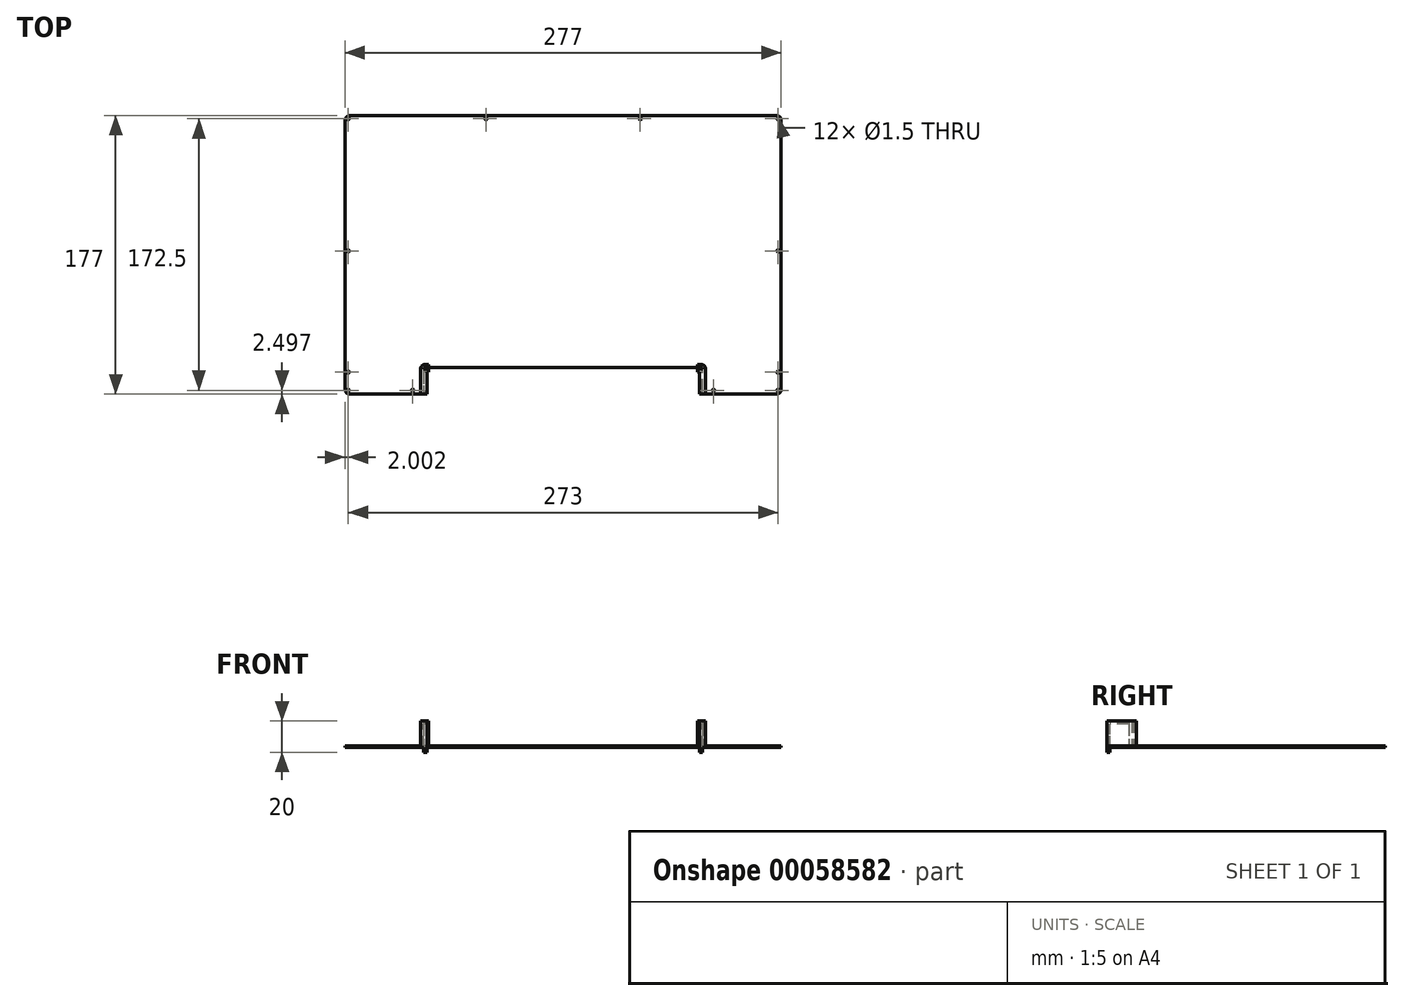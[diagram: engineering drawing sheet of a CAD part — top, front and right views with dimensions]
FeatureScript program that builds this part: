
annotation { "Feature Type Name" : "Feature", "Feature Type Description" : "" }
export const myFeature = defineFeature(function(context is Context, id is Id, definition is map)
    precondition{}
    {
        {
            var Q0;
            Q0=qCreatedBy(makeId("Top.planeOp"),FACE);
            var sketch = newSketch(context, id + "F0", { "sketchPlane" : qUnion([Q0])});
            skLineSegment(sketch, "E0.0.0", {"start": v(88.9, -46.67) * mm, "end": v(88.9, -105.67) * mm});
            skLineSegment(sketch, "E0.0.1", {"start": v(88.9, -105.67) * mm, "end": v(-89.1, -105.67) * mm});
            skLineSegment(sketch, "E0.0.2", {"start": v(-89.1, -105.67) * mm, "end": v(-89.1, -46.67) * mm});
            skLineSegment(sketch, "E0.0.3", {"start": v(-89.1, -46.67) * mm, "end": v(-86.1, -46.67) * mm});
            skLineSegment(sketch, "E0.0.4", {"start": v(-86.1, -46.67) * mm, "end": v(-86.1, -44.67) * mm});
            skLineSegment(sketch, "E0.0.5", {"start": v(-86.1, -44.67) * mm, "end": v(-89.1, -44.67) * mm});
            skLineSegment(sketch, "E0.0.6", {"start": v(-89.1, -44.67) * mm, "end": v(-89.1, -42.67) * mm});
            skLineSegment(sketch, "E0.0.7", {"start": v(-89.1, -42.67) * mm, "end": v(-86.1, -42.67) * mm});
            skLineSegment(sketch, "E0.0.8", {"start": v(-86.1, -42.67) * mm, "end": v(-86.1, -40.67) * mm});
            skLineSegment(sketch, "E0.0.9", {"start": v(-86.1, -40.67) * mm, "end": v(-91.1, -40.67) * mm});
            skLineSegment(sketch, "E0.0.10", {"start": v(-91.1, -40.67) * mm, "end": v(-91.1, -59.67) * mm});
            skLineSegment(sketch, "E0.0.11", {"start": v(-91.1, -59.67) * mm, "end": v(-137.1, -59.67) * mm});
            skLineSegment(sketch, "E0.0.12", {"start": v(-137.1, -59.67) * mm, "end": v(-137.1, -107.67) * mm});
            skLineSegment(sketch, "E0.0.13", {"start": v(-137.1, -107.67) * mm, "end": v(136.9, -107.67) * mm});
            skLineSegment(sketch, "E0.0.14", {"start": v(136.9, -107.67) * mm, "end": v(136.9, -59.67) * mm});
            skLineSegment(sketch, "E0.0.15", {"start": v(136.9, -59.67) * mm, "end": v(90.9, -59.67) * mm});
            skLineSegment(sketch, "E0.0.16", {"start": v(90.9, -59.67) * mm, "end": v(90.9, -40.67) * mm});
            skLineSegment(sketch, "E0.0.17", {"start": v(90.9, -40.67) * mm, "end": v(85.9, -40.67) * mm});
            skLineSegment(sketch, "E0.0.18", {"start": v(85.9, -40.67) * mm, "end": v(85.9, -42.67) * mm});
            skLineSegment(sketch, "E0.0.19", {"start": v(85.9, -42.67) * mm, "end": v(88.9, -42.67) * mm});
            skLineSegment(sketch, "E0.0.20", {"start": v(88.9, -42.67) * mm, "end": v(88.9, -44.67) * mm});
            skLineSegment(sketch, "E0.0.21", {"start": v(88.9, -44.67) * mm, "end": v(85.9, -44.67) * mm});
            skLineSegment(sketch, "E0.0.22", {"start": v(85.9, -44.67) * mm, "end": v(85.9, -46.67) * mm});
            skLineSegment(sketch, "E0.0.23", {"start": v(85.9, -46.67) * mm, "end": v(88.9, -46.67) * mm});
            skLineSegment(sketch, "E1.0.0", {"start": v(134.9, -59.67) * mm, "end": v(136.9, -59.67) * mm});
            skLineSegment(sketch, "E1.0.1", {"start": v(136.9, -59.67) * mm, "end": v(136.9, 110.83) * mm});
            skLineSegment(sketch, "E1.0.2", {"start": v(136.9, 110.83) * mm, "end": v(-137.1, 110.83) * mm});
            skLineSegment(sketch, "E1.0.3", {"start": v(-137.1, 110.83) * mm, "end": v(-137.1, -59.67) * mm});
            skLineSegment(sketch, "E1.0.4", {"start": v(-137.1, -59.67) * mm, "end": v(-135.1, -59.67) * mm});
            skLineSegment(sketch, "E1.0.5", {"start": v(-135.1, -59.67) * mm, "end": v(-135.1, -52.17) * mm});
            skLineSegment(sketch, "E1.0.6", {"start": v(-135.1, -52.17) * mm, "end": v(-130.1, -52.17) * mm});
            skLineSegment(sketch, "E1.0.7", {"start": v(-130.1, -52.17) * mm, "end": v(-130.1, -50.17) * mm});
            skLineSegment(sketch, "E1.0.8", {"start": v(-130.1, -50.17) * mm, "end": v(-134.1, -50.17) * mm});
            skLineSegment(sketch, "E1.0.9", {"start": v(-134.1, -50.17) * mm, "end": v(-134.1, -47.17) * mm});
            skLineSegment(sketch, "E1.0.10", {"start": v(-134.1, -47.17) * mm, "end": v(-135.1, -47.17) * mm});
            skLineSegment(sketch, "E1.0.11", {"start": v(-135.1, -47.17) * mm, "end": v(-135.1, 25.83) * mm});
            skLineSegment(sketch, "E1.0.12", {"start": v(-135.1, 25.83) * mm, "end": v(-134.1, 25.83) * mm});
            skLineSegment(sketch, "E1.0.13", {"start": v(-134.1, 25.83) * mm, "end": v(-134.1, 30.83) * mm});
            skLineSegment(sketch, "E1.0.14", {"start": v(-134.1, 30.83) * mm, "end": v(-135.1, 30.83) * mm});
            skLineSegment(sketch, "E1.0.15", {"start": v(-135.1, 30.83) * mm, "end": v(-135.1, 103.83) * mm});
            skLineSegment(sketch, "E1.0.16", {"start": v(-135.1, 103.83) * mm, "end": v(-134.1, 103.83) * mm});
            skLineSegment(sketch, "E1.0.17", {"start": v(-134.1, 103.83) * mm, "end": v(-134.1, 106.83) * mm});
            skLineSegment(sketch, "E1.0.18", {"start": v(-134.1, 106.83) * mm, "end": v(-129.1, 106.83) * mm});
            skLineSegment(sketch, "E1.0.19", {"start": v(-129.1, 106.83) * mm, "end": v(-129.1, 108.83) * mm});
            skLineSegment(sketch, "E1.0.20", {"start": v(-129.1, 108.83) * mm, "end": v(-50.1, 108.83) * mm});
            skLineSegment(sketch, "E1.0.21", {"start": v(-50.1, 108.83) * mm, "end": v(-50.1, 106.83) * mm});
            skLineSegment(sketch, "E1.0.22", {"start": v(-50.1, 106.83) * mm, "end": v(-45.1, 106.83) * mm});
            skLineSegment(sketch, "E1.0.23", {"start": v(-45.1, 106.83) * mm, "end": v(-45.1, 108.83) * mm});
            skLineSegment(sketch, "E1.0.24", {"start": v(-45.1, 108.83) * mm, "end": v(44.9, 108.83) * mm});
            skLineSegment(sketch, "E1.0.25", {"start": v(44.9, 108.83) * mm, "end": v(44.9, 106.83) * mm});
            skLineSegment(sketch, "E1.0.26", {"start": v(44.9, 106.83) * mm, "end": v(49.9, 106.83) * mm});
            skLineSegment(sketch, "E1.0.27", {"start": v(49.9, 106.83) * mm, "end": v(49.9, 108.83) * mm});
            skLineSegment(sketch, "E1.0.28", {"start": v(49.9, 108.83) * mm, "end": v(128.9, 108.83) * mm});
            skLineSegment(sketch, "E1.0.29", {"start": v(128.9, 108.83) * mm, "end": v(128.9, 106.83) * mm});
            skLineSegment(sketch, "E1.0.30", {"start": v(128.9, 106.83) * mm, "end": v(133.9, 106.83) * mm});
            skLineSegment(sketch, "E1.0.31", {"start": v(133.9, 106.83) * mm, "end": v(133.9, 103.83) * mm});
            skLineSegment(sketch, "E1.0.32", {"start": v(133.9, 103.83) * mm, "end": v(134.9, 103.83) * mm});
            skLineSegment(sketch, "E1.0.33", {"start": v(134.9, 103.83) * mm, "end": v(134.9, 30.83) * mm});
            skLineSegment(sketch, "E1.0.34", {"start": v(134.9, 30.83) * mm, "end": v(133.9, 30.83) * mm});
            skLineSegment(sketch, "E1.0.35", {"start": v(133.9, 30.83) * mm, "end": v(133.9, 25.83) * mm});
            skLineSegment(sketch, "E1.0.36", {"start": v(133.9, 25.83) * mm, "end": v(134.9, 25.83) * mm});
            skLineSegment(sketch, "E1.0.37", {"start": v(134.9, 25.83) * mm, "end": v(134.9, -47.17) * mm});
            skLineSegment(sketch, "E1.0.38", {"start": v(134.9, -47.17) * mm, "end": v(133.9, -47.17) * mm});
            skLineSegment(sketch, "E1.0.39", {"start": v(133.9, -47.17) * mm, "end": v(133.9, -50.17) * mm});
            skLineSegment(sketch, "E1.0.40", {"start": v(133.9, -50.17) * mm, "end": v(129.9, -50.17) * mm});
            skLineSegment(sketch, "E1.0.41", {"start": v(129.9, -50.17) * mm, "end": v(129.9, -52.17) * mm});
            skLineSegment(sketch, "E1.0.42", {"start": v(129.9, -52.17) * mm, "end": v(134.9, -52.17) * mm});
            skLineSegment(sketch, "E1.0.43", {"start": v(134.9, -52.17) * mm, "end": v(134.9, -59.67) * mm});
            skLineSegment(sketch, "E2", {"start": v(-89.1, -105.67) * mm, "end": v(-89.1, -107.67) * mm});
            skLineSegment(sketch, "E3", {"start": v(88.9, -105.67) * mm, "end": v(88.9, -107.67) * mm});
            skSolve(sketch);
        }
        {
            var Q0;
            Q0=qCreatedBy(makeId("Top.planeOp"),FACE);
            var sketch = newSketch(context, id + "F1", { "sketchPlane" : qUnion([Q0])});
            skPoint(sketch, "E4.0", {"position": v(-91.1, -59.67) * mm});
            skPoint(sketch, "E5.0", {"position": v(-91.1, -40.67) * mm});
            skPoint(sketch, "E6.0", {"position": v(-86.1, -40.67) * mm});
            skPoint(sketch, "E7.0", {"position": v(-86.1, -42.67) * mm});
            skPoint(sketch, "E8.0", {"position": v(-89.1, -42.67) * mm});
            skPoint(sketch, "E9.0", {"position": v(-89.1, -46.67) * mm});
            skLineSegment(sketch, "E10", {"start": v(-91.1, -59.67) * mm, "end": v(-91.1, -40.67) * mm});
            skLineSegment(sketch, "E11", {"start": v(-91.1, -40.67) * mm, "end": v(-86.1, -40.67) * mm});
            skLineSegment(sketch, "E12", {"start": v(-86.1, -40.67) * mm, "end": v(-86.1, -42.67) * mm});
            skLineSegment(sketch, "E13", {"start": v(-86.1, -42.67) * mm, "end": v(-89.1, -42.67) * mm});
            skLineSegment(sketch, "E14", {"start": v(-89.1, -42.67) * mm, "end": v(-89.1, -43.67) * mm});
            skLineSegment(sketch, "E15", {"start": v(-89.1, -43.67) * mm, "end": v(-86.1, -43.67) * mm});
            skLineSegment(sketch, "E16", {"start": v(-86.1, -43.67) * mm, "end": v(-86.1, -45.67) * mm});
            skLineSegment(sketch, "E17", {"start": v(-86.1, -45.67) * mm, "end": v(-89.1, -45.67) * mm});
            skLineSegment(sketch, "E18", {"start": v(-89.1, -45.67) * mm, "end": v(-89.1, -59.67) * mm});
            skLineSegment(sketch, "E19", {"start": v(-89.1, -59.67) * mm, "end": v(-91.1, -59.67) * mm});
            skLineSegment(sketch, "E20", {"start": v(-89.1, -59.67) * mm, "end": v(-0.6, -59.67) * mm, "construction": true});
            skLineSegment(sketch, "E21", {"start": v(-0.6, -59.67) * mm, "end": v(-0.6, -8.93) * mm, "construction": true});
            skLineSegment(sketch, "E22.MirrorCS", {"start": v(87.9, -42.67) * mm, "end": v(87.9, -43.67) * mm});
            skLineSegment(sketch, "E23.MirrorCS", {"start": v(84.9, -43.67) * mm, "end": v(84.9, -45.67) * mm});
            skLineSegment(sketch, "E24.MirrorCS", {"start": v(84.9, -40.67) * mm, "end": v(84.9, -42.67) * mm});
            skLineSegment(sketch, "E25.MirrorCS", {"start": v(87.9, -59.67) * mm, "end": v(89.9, -59.67) * mm});
            skPoint(sketch, "E26.MirrorP", {"position": v(89.9, -59.67) * mm});
            skPoint(sketch, "E27.MirrorP", {"position": v(87.9, -46.67) * mm});
            skLineSegment(sketch, "E28.MirrorCS", {"start": v(87.9, -59.67) * mm, "end": v(-0.6, -59.67) * mm, "construction": true});
            skPoint(sketch, "E29.MirrorP", {"position": v(84.9, -42.67) * mm});
            skPoint(sketch, "E30.MirrorP", {"position": v(84.9, -40.67) * mm});
            skLineSegment(sketch, "E31.MirrorCS", {"start": v(89.9, -59.67) * mm, "end": v(89.9, -40.67) * mm});
            skLineSegment(sketch, "E32.MirrorCS", {"start": v(89.9, -40.67) * mm, "end": v(84.9, -40.67) * mm});
            skLineSegment(sketch, "E33.MirrorCS", {"start": v(84.9, -42.67) * mm, "end": v(87.9, -42.67) * mm});
            skLineSegment(sketch, "E34.MirrorCS", {"start": v(87.9, -43.67) * mm, "end": v(84.9, -43.67) * mm});
            skLineSegment(sketch, "E35.MirrorCS", {"start": v(84.9, -45.67) * mm, "end": v(87.9, -45.67) * mm});
            skLineSegment(sketch, "E36.MirrorCS", {"start": v(87.9, -45.67) * mm, "end": v(87.9, -59.67) * mm});
            skPoint(sketch, "E37.MirrorP", {"position": v(87.9, -42.67) * mm});
            skPoint(sketch, "E38.MirrorP", {"position": v(89.9, -40.67) * mm});
            skSolve(sketch);
        }
        {
            var Q0;
            Q0 = qSketchRegion(id + "F1", true);
            extrude(context, id + "F2", {"entities" : qUnion([Q0]), "depth" : 16 * mm});
        }
        {
            var Q0;
            Q0=qCreatedBy(makeId("Top.planeOp"),FACE);
            var sketch = newSketch(context, id + "F3", { "sketchPlane" : qUnion([Q0])});
            skPoint(sketch, "E39.0", {"position": v(-89.1, -59.67) * mm});
            skLineSegment(sketch, "E40", {"start": v(-89.1, -59.67) * mm, "end": v(-139.1, -59.67) * mm});
            skLineSegment(sketch, "E41", {"start": v(-139.1, -59.67) * mm, "end": v(-139.1, 117.33) * mm});
            skLineSegment(sketch, "E42", {"start": v(-139.1, 117.33) * mm, "end": v(137.9, 117.33) * mm});
            skPoint(sketch, "E43.0", {"position": v(87.9, -59.67) * mm});
            skLineSegment(sketch, "E44", {"start": v(137.9, 117.33) * mm, "end": v(137.9, -59.67) * mm});
            skLineSegment(sketch, "E45", {"start": v(137.9, -59.67) * mm, "end": v(87.9, -59.67) * mm});
            skPoint(sketch, "E46.0", {"position": v(-89.1, -42.67) * mm});
            skPoint(sketch, "E47.0", {"position": v(87.9, -42.67) * mm});
            skLineSegment(sketch, "E48", {"start": v(87.9, -59.67) * mm, "end": v(87.9, -42.67) * mm});
            skLineSegment(sketch, "E49", {"start": v(87.9, -42.67) * mm, "end": v(-89.1, -42.67) * mm});
            skLineSegment(sketch, "E50", {"start": v(-89.1, -42.67) * mm, "end": v(-89.1, -59.67) * mm});
            skSolve(sketch);
        }
        {
            var Q0;
            Q0 = qSketchRegion(id + "F3", true);
            extrude(context, id + "F4", {"entities" : qUnion([Q0]), "operationType" : NewBodyOperationType.ADD, "oppositeDirection" : true, "depth" : 1 * mm});
        }
        {
            var Q0;
            Q0=makeQuery(id+"F2.opExtrude","CAP_FACE",FACE,{"disambiguationData":[OSD([sQuery(id+"F1.wireOp",EDGE,"E10"),sQuery(id+"F1.wireOp",EDGE,"E11"),sQuery(id+"F1.wireOp",EDGE,"E12"),sQuery(id+"F1.wireOp",EDGE,"E13"),sQuery(id+"F1.wireOp",EDGE,"E14"),sQuery(id+"F1.wireOp",EDGE,"E15"),sQuery(id+"F1.wireOp",EDGE,"E16"),sQuery(id+"F1.wireOp",EDGE,"E17"),sQuery(id+"F1.wireOp",EDGE,"E18"),sQuery(id+"F1.wireOp",EDGE,"E19")])],"isStart":false});
            var sketch = newSketch(context, id + "F5", { "sketchPlane" : qUnion([Q0])});
            skLineSegment(sketch, "E51.bottom", {"start": v(-89.1, -59.67) * mm, "end": v(-87.1, -59.67) * mm});
            skLineSegment(sketch, "E51.top", {"start": v(-89.1, -57.67) * mm, "end": v(-87.1, -57.67) * mm});
            skLineSegment(sketch, "E51.left", {"start": v(-89.1, -59.67) * mm, "end": v(-89.1, -57.67) * mm});
            skLineSegment(sketch, "E51.right", {"start": v(-87.1, -59.67) * mm, "end": v(-87.1, -57.67) * mm});
            skPoint(sketch, "E52.0", {"position": v(87.9, -59.67) * mm});
            skLineSegment(sketch, "E53.bottom", {"start": v(87.9, -59.67) * mm, "end": v(85.9, -59.67) * mm});
            skLineSegment(sketch, "E53.top", {"start": v(87.9, -57.67) * mm, "end": v(85.9, -57.67) * mm});
            skLineSegment(sketch, "E53.left", {"start": v(87.9, -59.67) * mm, "end": v(87.9, -57.67) * mm});
            skLineSegment(sketch, "E53.right", {"start": v(85.9, -59.67) * mm, "end": v(85.9, -57.67) * mm});
            skSolve(sketch);
        }
        {
            var Q0;
            Q0 = qSketchRegion(id + "F5", true);
            extrude(context, id + "F6", {"entities" : qUnion([Q0]), "operationType" : NewBodyOperationType.ADD, "oppositeDirection" : true, "depth" : 20 * mm});
        }
        {
            var Q0;
            Q0=makeQuery(id+"F6.boolean.opBoolean","MERGE",FACE,{"derivedFrom":[makeQuery(id+"F2.opExtrude","CAP_FACE",FACE,{"disambiguationData":[OSD([sQuery(id+"F1.wireOp",EDGE,"E10"),sQuery(id+"F1.wireOp",EDGE,"E11"),sQuery(id+"F1.wireOp",EDGE,"E12"),sQuery(id+"F1.wireOp",EDGE,"E13"),sQuery(id+"F1.wireOp",EDGE,"E14"),sQuery(id+"F1.wireOp",EDGE,"E15"),sQuery(id+"F1.wireOp",EDGE,"E16"),sQuery(id+"F1.wireOp",EDGE,"E17"),sQuery(id+"F1.wireOp",EDGE,"E18"),sQuery(id+"F1.wireOp",EDGE,"E19")])],"isStart":false}),makeQuery(id+"F6.opExtrude","CAP_FACE",FACE,{"disambiguationData":[OSD([sQuery(id+"F5.wireOp",EDGE,"E51.bottom"),sQuery(id+"F5.wireOp",EDGE,"E51.top"),sQuery(id+"F5.wireOp",EDGE,"E51.left"),sQuery(id+"F5.wireOp",EDGE,"E51.right")])],"isStart":true})]});
            var sketch = newSketch(context, id + "F7", { "sketchPlane" : qUnion([Q0])});
            skLineSegment(sketch, "E54.bottom", {"start": v(-87.1, -57.67) * mm, "end": v(-89.1, -57.67) * mm});
            skLineSegment(sketch, "E54.top", {"start": v(-87.1, -45.67) * mm, "end": v(-89.1, -45.67) * mm});
            skLineSegment(sketch, "E54.left", {"start": v(-87.1, -57.67) * mm, "end": v(-87.1, -45.67) * mm});
            skLineSegment(sketch, "E54.right", {"start": v(-89.1, -57.67) * mm, "end": v(-89.1, -45.67) * mm});
            skPoint(sketch, "E55.0", {"position": v(87.9, -45.67) * mm});
            skPoint(sketch, "E56.0", {"position": v(85.9, -57.67) * mm});
            skLineSegment(sketch, "E57.bottom", {"start": v(85.9, -57.67) * mm, "end": v(87.9, -57.67) * mm});
            skLineSegment(sketch, "E57.top", {"start": v(85.9, -45.67) * mm, "end": v(87.9, -45.67) * mm});
            skLineSegment(sketch, "E57.left", {"start": v(85.9, -57.67) * mm, "end": v(85.9, -45.67) * mm});
            skLineSegment(sketch, "E57.right", {"start": v(87.9, -57.67) * mm, "end": v(87.9, -45.67) * mm});
            skSolve(sketch);
        }
        {
            var Q0;
            Q0 = qSketchRegion(id + "F7", true);
            extrude(context, id + "F8", {"entities" : qUnion([Q0]), "operationType" : NewBodyOperationType.ADD, "oppositeDirection" : true, "depth" : 2 * mm});
        }
        {
            var Q0;
            Q0=makeQuery(id+"F4.opExtrude","CAP_FACE",FACE,{"disambiguationData":[OSD([sQuery(id+"F3.wireOp",EDGE,"E40"),sQuery(id+"F3.wireOp",EDGE,"E41"),sQuery(id+"F3.wireOp",EDGE,"E42"),sQuery(id+"F3.wireOp",EDGE,"E44"),sQuery(id+"F3.wireOp",EDGE,"E45"),sQuery(id+"F3.wireOp",EDGE,"E48"),sQuery(id+"F3.wireOp",EDGE,"E49"),sQuery(id+"F3.wireOp",EDGE,"E50")])],"isStart":true});
            var sketch = newSketch(context, id + "F9", { "sketchPlane" : qUnion([Q0])});
            skPoint(sketch, "E58", {"position": v(-137.1, 115.33) * mm});
            skPoint(sketch, "E59", {"position": v(-49.6, 115.33) * mm});
            skPoint(sketch, "E60", {"position": v(-137.1, 31.33) * mm});
            skPoint(sketch, "E61", {"position": v(-137.1, -45.67) * mm});
            skPoint(sketch, "E62", {"position": v(-137.1, -57.17) * mm});
            skPoint(sketch, "E63", {"position": v(-96.1, -57.17) * mm});
            skLineSegment(sketch, "E64", {"start": v(-0.6, 117.33) * mm, "end": v(-0.6, -23.18) * mm, "construction": true});
            skPoint(sketch, "E65.MirrorP", {"position": v(94.9, -57.17) * mm});
            skPoint(sketch, "E66.MirrorP", {"position": v(135.9, -57.17) * mm});
            skPoint(sketch, "E67.MirrorP", {"position": v(48.4, 115.33) * mm});
            skPoint(sketch, "E68.MirrorP", {"position": v(135.9, 115.33) * mm});
            skPoint(sketch, "E69.MirrorP", {"position": v(135.9, 31.33) * mm});
            skPoint(sketch, "E70.MirrorP", {"position": v(135.9, -45.67) * mm});
            skSolve(sketch);
        }
        {
            var Q0;
            Q0=sQuery(id+"F9.wireOp",VERTEX,"E59");
            var Q1;
            Q1=sQuery(id+"F9.wireOp",VERTEX,"E60");
            var Q2;
            Q2=sQuery(id+"F9.wireOp",VERTEX,"E62");
            var Q3;
            Q3=sQuery(id+"F9.wireOp",VERTEX,"E61");
            var Q4;
            Q4=sQuery(id+"F9.wireOp",VERTEX,"E58");
            var Q5;
            Q5=sQuery(id+"F9.wireOp",VERTEX,"E70.MirrorP");
            var Q6;
            Q6=sQuery(id+"F9.wireOp",VERTEX,"E63");
            var Q7;
            Q7=sQuery(id+"F9.wireOp",VERTEX,"E65.MirrorP");
            var Q8;
            Q8=sQuery(id+"F9.wireOp",VERTEX,"E66.MirrorP");
            var Q9;
            Q9=sQuery(id+"F9.wireOp",VERTEX,"E67.MirrorP");
            var Q10;
            Q10=sQuery(id+"F9.wireOp",VERTEX,"E68.MirrorP");
            var Q11;
            Q11=sQuery(id+"F9.wireOp",VERTEX,"E69.MirrorP");
            var Q12;
            Q12=makeQuery(id+"F2.opExtrude","SWEPT_BODY",BODY,{"disambiguationData":[OSD([sQuery(id+"F1.wireOp",EDGE,"E10"),sQuery(id+"F1.wireOp",EDGE,"E11"),sQuery(id+"F1.wireOp",EDGE,"E12"),sQuery(id+"F1.wireOp",EDGE,"E13"),sQuery(id+"F1.wireOp",EDGE,"E14"),sQuery(id+"F1.wireOp",EDGE,"E15"),sQuery(id+"F1.wireOp",EDGE,"E16"),sQuery(id+"F1.wireOp",EDGE,"E17"),sQuery(id+"F1.wireOp",EDGE,"E18"),sQuery(id+"F1.wireOp",EDGE,"E19")])]});
            hole(context, id + "F10", {"style" : HoleStyle.SIMPLE, "holeDiameter" : 1.5 * mm, "endStyle" : HoleEndStyle.THROUGH, "locations" : qUnion([Q0, Q1, Q2, Q3, Q4, Q5, Q6, Q7, Q8, Q9, Q10, Q11]), "scope" : qUnion([Q12])});
        }
        {
            var Q0;
            Q0=makeQuery(id+"F4.opExtrude","SWEPT_EDGE",EDGE,{"disambiguationData":[OSD([sQuery(id+"F3.wireOp",EDGE,"E41"),sQuery(id+"F3.wireOp",EDGE,"E42")])]});
            var Q1;
            Q1=makeQuery(id+"F4.opExtrude","SWEPT_EDGE",EDGE,{"disambiguationData":[OSD([sQuery(id+"F3.wireOp",EDGE,"E42"),sQuery(id+"F3.wireOp",EDGE,"E44")])]});
            var Q2;
            Q2=makeQuery(id+"F2.opExtrude","SWEPT_EDGE",EDGE,{"disambiguationData":[OSD([sQuery(id+"F1.wireOp",EDGE,"E10"),sQuery(id+"F1.wireOp",EDGE,"E11")])]});
            var Q3;
            Q3=makeQuery(id+"F4.opExtrude","SWEPT_EDGE",EDGE,{"disambiguationData":[OSD([sQuery(id+"F3.wireOp",EDGE,"E40"),sQuery(id+"F3.wireOp",EDGE,"E41")])]});
            var Q4;
            Q4=makeQuery(id+"F2.opExtrude","SWEPT_EDGE",EDGE,{"disambiguationData":[OSD([sQuery(id+"F1.wireOp",EDGE,"E31.MirrorCS"),sQuery(id+"F1.wireOp",EDGE,"E32.MirrorCS")])]});
            var Q5;
            Q5=makeQuery(id+"F4.opExtrude","SWEPT_EDGE",EDGE,{"disambiguationData":[OSD([sQuery(id+"F3.wireOp",EDGE,"E44"),sQuery(id+"F3.wireOp",EDGE,"E45")])]});
            fillet(context, id + "F11", {"entities" : qUnion([Q0, Q1, Q2, Q3, Q4, Q5]), "radius" : 3 * mm, "tangentPropagation" : true, "allowEdgeOverflow" : false});
        }
    });
